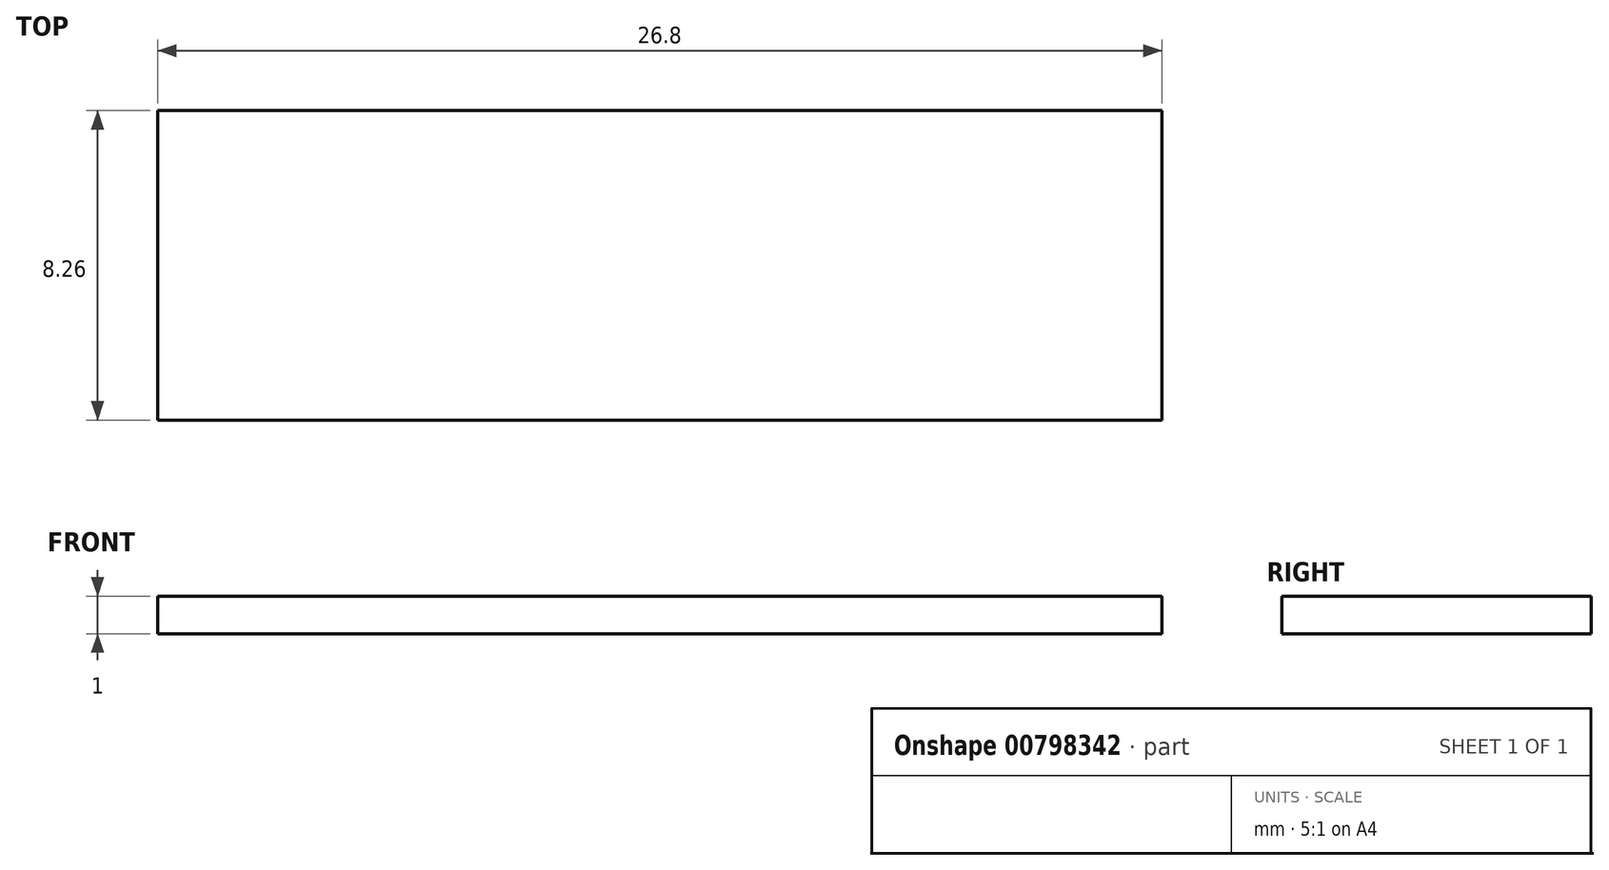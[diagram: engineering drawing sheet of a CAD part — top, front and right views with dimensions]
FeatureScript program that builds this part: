
annotation { "Feature Type Name" : "Feature", "Feature Type Description" : "" }
export const myFeature = defineFeature(function(context is Context, id is Id, definition is map)
    precondition{}
    {
        {
            var Q0;
            Q0=qCreatedBy(makeId("Top.planeOp"),FACE);
            var sketch = newSketch(context, id + "F0", { "sketchPlane" : qUnion([Q0])});
            skLineSegment(sketch, "E0.bottom", {"start": v(0, 0) * mm, "end": v(-26.8, 0) * mm});
            skLineSegment(sketch, "E0.top", {"start": v(0, 8.26) * mm, "end": v(-26.8, 8.26) * mm});
            skLineSegment(sketch, "E0.left", {"start": v(0, 0) * mm, "end": v(0, 8.26) * mm});
            skLineSegment(sketch, "E0.right", {"start": v(-26.8, 0) * mm, "end": v(-26.8, 8.26) * mm});
            skSolve(sketch);
        }
        {
            var Q0;
            Q0=makeQuery(id+"F0.imprint","IMPRINT",FACE,{"disambiguationData":[TD([[makeQuery(id+"F0.imprint","IMPRINT",EDGE,{"derivedFrom":sQuery(id+"F0.wireOp",EDGE,"E0.bottom")}),-1.0]])]});
            extrude(context, id + "F1", {"entities" : qUnion([Q0]), "depth" : 1 * mm, "offsetDistance" : 25 * mm});
        }
    });
